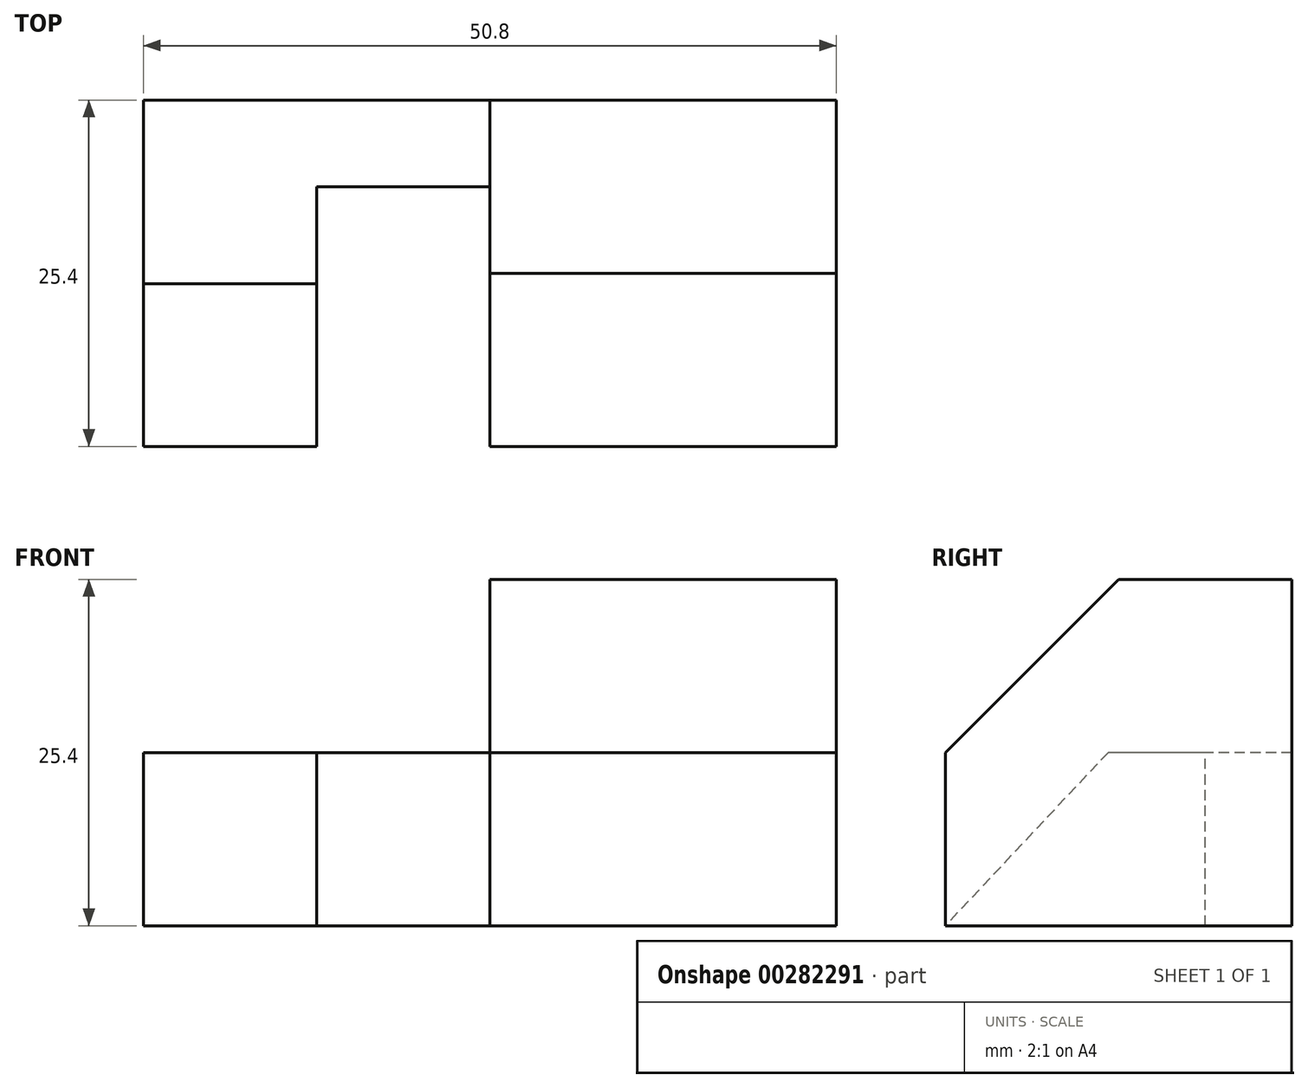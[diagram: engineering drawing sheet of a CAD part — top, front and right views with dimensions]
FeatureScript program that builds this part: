
annotation { "Feature Type Name" : "Feature", "Feature Type Description" : "" }
export const myFeature = defineFeature(function(context is Context, id is Id, definition is map)
    precondition{}
    {
        {
            var Q0;
            Q0=qCreatedBy(makeId("Right.planeOp"),FACE);
            var sketch = newSketch(context, id + "F0", { "sketchPlane" : qUnion([Q0])});
            skLineSegment(sketch, "E0", {"start": v(0, 0) * mm, "end": v(0, 25.4) * mm});
            skLineSegment(sketch, "E1", {"start": v(0, 25.4) * mm, "end": v(-12.7, 25.4) * mm});
            skLineSegment(sketch, "E2", {"start": v(-12.7, 25.4) * mm, "end": v(-25.4, 12.7) * mm});
            skLineSegment(sketch, "E3", {"start": v(-25.4, 12.7) * mm, "end": v(-25.4, 0) * mm});
            skLineSegment(sketch, "E4", {"start": v(-25.4, 0) * mm, "end": v(0, 0) * mm});
            skSolve(sketch);
        }
        {
            var Q0;
            Q0 = qSketchRegion(id + "F0", true);
            extrude(context, id + "F1", {"entities" : qUnion([Q0]), "depth" : 25.4 * mm});
        }
        {
            var Q0;
            Q0=makeQuery(id+"F1.opExtrude","CAP_FACE",FACE,{"disambiguationData":[OSD([sQuery(id+"F0.wireOp",EDGE,"E0"),sQuery(id+"F0.wireOp",EDGE,"E1"),sQuery(id+"F0.wireOp",EDGE,"E2"),sQuery(id+"F0.wireOp",EDGE,"E3"),sQuery(id+"F0.wireOp",EDGE,"E4")])],"isStart":true});
            var sketch = newSketch(context, id + "F2", { "sketchPlane" : qUnion([Q0])});
            skLineSegment(sketch, "E5.bottom", {"start": v(0, 0) * mm, "end": v(6.35, 0) * mm});
            skLineSegment(sketch, "E5.top", {"start": v(0, 12.7) * mm, "end": v(6.35, 12.7) * mm});
            skLineSegment(sketch, "E5.left", {"start": v(0, 0) * mm, "end": v(0, 12.7) * mm});
            skLineSegment(sketch, "E5.right", {"start": v(6.35, 0) * mm, "end": v(6.35, 12.7) * mm});
            skSolve(sketch);
        }
        {
            var Q0;
            Q0 = qSketchRegion(id + "F2", true);
            extrude(context, id + "F3", {"entities" : qUnion([Q0]), "operationType" : NewBodyOperationType.ADD, "depth" : 25.4 * mm});
        }
        {
            var Q0;
            Q0=makeQuery(id+"F3.opExtrude","CAP_FACE",FACE,{"disambiguationData":[OSD([sQuery(id+"F2.wireOp",EDGE,"E5.bottom"),sQuery(id+"F2.wireOp",EDGE,"E5.top"),sQuery(id+"F2.wireOp",EDGE,"E5.left"),sQuery(id+"F2.wireOp",EDGE,"E5.right")])],"isStart":false});
            var sketch = newSketch(context, id + "F4", { "sketchPlane" : qUnion([Q0])});
            skLineSegment(sketch, "E6", {"start": v(25.4, 0) * mm, "end": v(0, 0) * mm});
            skLineSegment(sketch, "E7", {"start": v(0, 12.7) * mm, "end": v(13.48, 12.7) * mm});
            skPoint(sketch, "E7.endSnap0", {"position": v(3.17, 12.7) * mm});
            skLineSegment(sketch, "E8", {"start": v(13.48, 12.7) * mm, "end": v(25.4, 0) * mm});
            skSolve(sketch);
        }
        {
            var Q0;
            Q0 = qSketchRegion(id + "F4", true);
            var Q1;
            {var subQ2=sQuery(id+"F4.wireOp",EDGE,"E8");Q1=makeQuery(id+"F4.imprint","IMPRINT",FACE,{"disambiguationData":[TD([[makeQuery(id+"F4.imprint","IMPRINT",EDGE,{"derivedFrom":subQ2}),-1.0]])]});}
            extrude(context, id + "F5", {"entities" : qUnion([Q0, Q1]), "operationType" : NewBodyOperationType.ADD, "oppositeDirection" : true, "depth" : 12.7 * mm});
        }
    });
